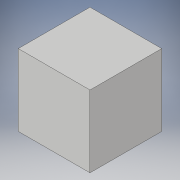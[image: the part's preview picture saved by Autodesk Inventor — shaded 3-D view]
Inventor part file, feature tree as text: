
AUTODESK INVENTOR PART (.ipt)
format: ipt  version: 2019 (Build 230136000, 136)  size: 206,336 bytes
history: native  units: mm
features: extrude x1, sketch x1
ambient origin geometry x8: Origin, YZ Plane, XZ Plane, XY Plane, X Axis, Y Axis, Z Axis, Center Point
bodies: Solid1 (feature_tree)
feature tree (2):
  extrude  "Extrusion1"  Depth=20.0mm
  sketch  "Sketch1"  dims[d0=20.0mm d1=20.0mm d2=20.0mm d3=0.0mm]
